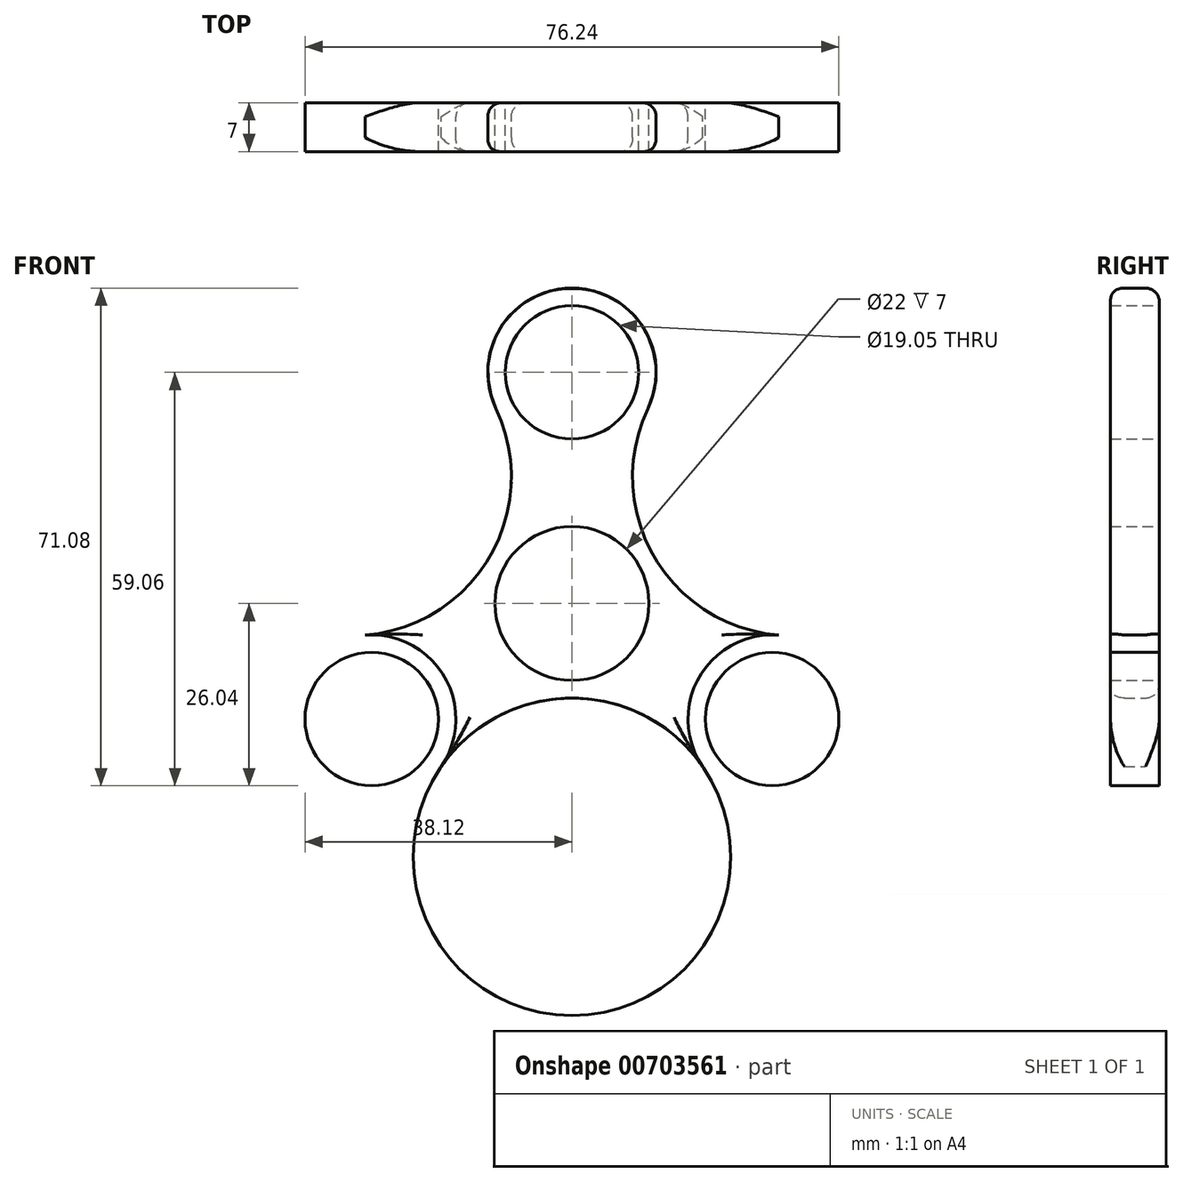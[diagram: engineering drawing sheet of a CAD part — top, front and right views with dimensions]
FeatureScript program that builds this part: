
annotation { "Feature Type Name" : "Feature", "Feature Type Description" : "" }
export const myFeature = defineFeature(function(context is Context, id is Id, definition is map)
    precondition{}
    {
        {
            var Q0;
            Q0=qCreatedBy(makeId("Front.planeOp"),FACE);
            var sketch = newSketch(context, id + "F0", { "sketchPlane" : qUnion([Q0])});
            skCircle(sketch, "E0", {"center": v(0, 0) * mm, "radius": 11 * mm});
            skCircle(sketch, "E1", {"center": v(0, 0) * mm, "radius": 13.5 * mm});
            skLineSegment(sketch, "E2", {"start": v(0, 0) * mm, "end": v(0, -44.01) * mm});
            skCircle(sketch, "E3.MirrorC", {"center": v(0, 33.02) * mm, "radius": 12.02 * mm});
            skCircle(sketch, "E4.MirrorC", {"center": v(0, 33.02) * mm, "radius": 9.53 * mm});
            skCircle(sketch, "E5.MirrorC", {"center": v(-28.6, -16.51) * mm, "radius": 9.53 * mm});
            skCircle(sketch, "E6.MirrorC", {"center": v(-28.6, -16.51) * mm, "radius": 12.02 * mm});
            skCircle(sketch, "E7.MirrorC", {"center": v(28.6, -16.5) * mm, "radius": 12.02 * mm});
            skCircle(sketch, "E8.MirrorC", {"center": v(28.6, -16.5) * mm, "radius": 9.53 * mm});
            skPoint(sketch, "E9", {"position": v(-11.7, 6.75) * mm});
            skArc(sketch, "E10", {"start": v(-29.5, -4.52) * mm, "mid": v(-11.7, 6.75) * mm, "end": v(-10.84, 27.81) * mm});
            skArc(sketch, "E11.MirrorCS", {"start": v(-18.67, -23.3) * mm, "mid": v(0, -13.5) * mm, "end": v(18.67, -23.3) * mm});
            skArc(sketch, "E12.MirrorCS", {"start": v(10.84, 27.81) * mm, "mid": v(11.7, 6.75) * mm, "end": v(29.5, -4.52) * mm});
            skSolve(sketch);
        }
        {
            var Q0;
            {var subQ0=sQuery(id+"F0.wireOp",EDGE,"E10");var subQ1=sQuery(id+"F0.wireOp",EDGE,"E1");var subQ2=makeQuery(id+"F0.imprint","INTERSECT",VERTEX,{"derivedFrom":[subQ1,subQ0]});Q0=makeQuery(id+"F0.imprint","IMPRINT",FACE,{"disambiguationData":[TD([[makeQuery(id+"F0.imprint","IMPRINT",EDGE,{"disambiguationData":[TD([[subQ2,1.0]])],"derivedFrom":subQ1}),-1.0]])]});}
            var Q1;
            {var subQ0=sQuery(id+"F0.wireOp",EDGE,"E10");var subQ1=sQuery(id+"F0.wireOp",EDGE,"E1");var subQ2=makeQuery(id+"F0.imprint","INTERSECT",VERTEX,{"derivedFrom":[subQ1,subQ0]});Q1=makeQuery(id+"F0.imprint","IMPRINT",FACE,{"disambiguationData":[TD([[makeQuery(id+"F0.imprint","IMPRINT",EDGE,{"disambiguationData":[TD([[subQ2,-1.0]])],"derivedFrom":subQ1}),-1.0]])]});}
            var Q2;
            {var subQ0=sQuery(id+"F0.wireOp",EDGE,"E12.MirrorCS");var subQ1=sQuery(id+"F0.wireOp",EDGE,"E1");var subQ2=makeQuery(id+"F0.imprint","INTERSECT",VERTEX,{"derivedFrom":[subQ1,subQ0]});Q2=makeQuery(id+"F0.imprint","IMPRINT",FACE,{"disambiguationData":[TD([[makeQuery(id+"F0.imprint","IMPRINT",EDGE,{"disambiguationData":[TD([[subQ2,1.0]])],"derivedFrom":subQ1}),-1.0]])]});}
            var Q3;
            Q3=makeQuery(id+"F0.imprint","IMPRINT",FACE,{"disambiguationData":[TD([[makeQuery(id+"F0.imprint","IMPRINT",EDGE,{"derivedFrom":sQuery(id+"F0.wireOp",EDGE,"E0")}),-1.0]])]});
            var Q4;
            Q4=makeQuery(id+"F0.imprint","IMPRINT",FACE,{"disambiguationData":[TD([[makeQuery(id+"F0.imprint","IMPRINT",EDGE,{"derivedFrom":sQuery(id+"F0.wireOp",EDGE,"E8.MirrorC")}),1.0]])]});
            var Q5;
            Q5=makeQuery(id+"F0.imprint","IMPRINT",FACE,{"disambiguationData":[TD([[makeQuery(id+"F0.imprint","IMPRINT",EDGE,{"derivedFrom":sQuery(id+"F0.wireOp",EDGE,"E5.MirrorC")}),1.0]])]});
            var Q6;
            Q6=makeQuery(id+"F0.imprint","IMPRINT",FACE,{"disambiguationData":[TD([[makeQuery(id+"F0.imprint","IMPRINT",EDGE,{"derivedFrom":sQuery(id+"F0.wireOp",EDGE,"E4.MirrorC")}),-1.0]])]});
            extrude(context, id + "F1", {"entities" : qUnion([Q0, Q1, Q2, Q3, Q4, Q5, Q6]), "depth" : 7 * mm, "offsetDistance" : 25.4 * mm});
        }
        {
            var Q0;
            Q0=makeQuery(id+"F1.opExtrude","CAP_EDGE",EDGE,{"disambiguationData":[OSD([sQuery(id+"F0.wireOp",EDGE,"E3.MirrorC")])],"isStart":false});
            var Q1;
            Q1=makeQuery(id+"F1.opExtrude","CAP_EDGE",EDGE,{"disambiguationData":[OSD([sQuery(id+"F0.wireOp",EDGE,"E12.MirrorCS")])],"isStart":false});
            var Q2;
            Q2=makeQuery(id+"F1.opExtrude","CAP_EDGE",EDGE,{"disambiguationData":[OSD([sQuery(id+"F0.wireOp",EDGE,"E7.MirrorC")])],"isStart":false});
            var Q3;
            Q3=makeQuery(id+"F1.opExtrude","CAP_EDGE",EDGE,{"disambiguationData":[OSD([sQuery(id+"F0.wireOp",EDGE,"E11.MirrorCS")])],"isStart":false});
            var Q4;
            Q4=makeQuery(id+"F1.opExtrude","CAP_EDGE",EDGE,{"disambiguationData":[OSD([sQuery(id+"F0.wireOp",EDGE,"E10")])],"isStart":false});
            var Q5;
            Q5=makeQuery(id+"F1.opExtrude","CAP_EDGE",EDGE,{"disambiguationData":[OSD([sQuery(id+"F0.wireOp",EDGE,"E6.MirrorC")])],"isStart":false});
            fillet(context, id + "F2", {"entities" : qUnion([Q0, Q1, Q2, Q3, Q4, Q5]), "radius" : 2 * mm, "rho" : 0.5, "crossSection" : FilletCrossSection.CONIC, "allowEdgeOverflow" : false});
        }
        {
            var Q0;
            Q0=makeQuery(id+"F1.opExtrude","CAP_EDGE",EDGE,{"disambiguationData":[OSD([sQuery(id+"F0.wireOp",EDGE,"E10")])],"isStart":true});
            var Q1;
            Q1=makeQuery(id+"F1.opExtrude","CAP_EDGE",EDGE,{"disambiguationData":[OSD([sQuery(id+"F0.wireOp",EDGE,"E3.MirrorC")])],"isStart":true});
            var Q2;
            Q2=makeQuery(id+"F1.opExtrude","CAP_EDGE",EDGE,{"disambiguationData":[OSD([sQuery(id+"F0.wireOp",EDGE,"E6.MirrorC")])],"isStart":true});
            var Q3;
            Q3=makeQuery(id+"F1.opExtrude","CAP_EDGE",EDGE,{"disambiguationData":[OSD([sQuery(id+"F0.wireOp",EDGE,"E11.MirrorCS")])],"isStart":true});
            var Q4;
            Q4=makeQuery(id+"F1.opExtrude","CAP_EDGE",EDGE,{"disambiguationData":[OSD([sQuery(id+"F0.wireOp",EDGE,"E12.MirrorCS")])],"isStart":true});
            var Q5;
            Q5=makeQuery(id+"F1.opExtrude","CAP_EDGE",EDGE,{"disambiguationData":[OSD([sQuery(id+"F0.wireOp",EDGE,"E7.MirrorC")])],"isStart":true});
            fillet(context, id + "F3", {"entities" : qUnion([Q0, Q1, Q2, Q3, Q4, Q5]), "radius" : 2 * mm, "tangentPropagation" : true, "allowEdgeOverflow" : false});
        }
    });
